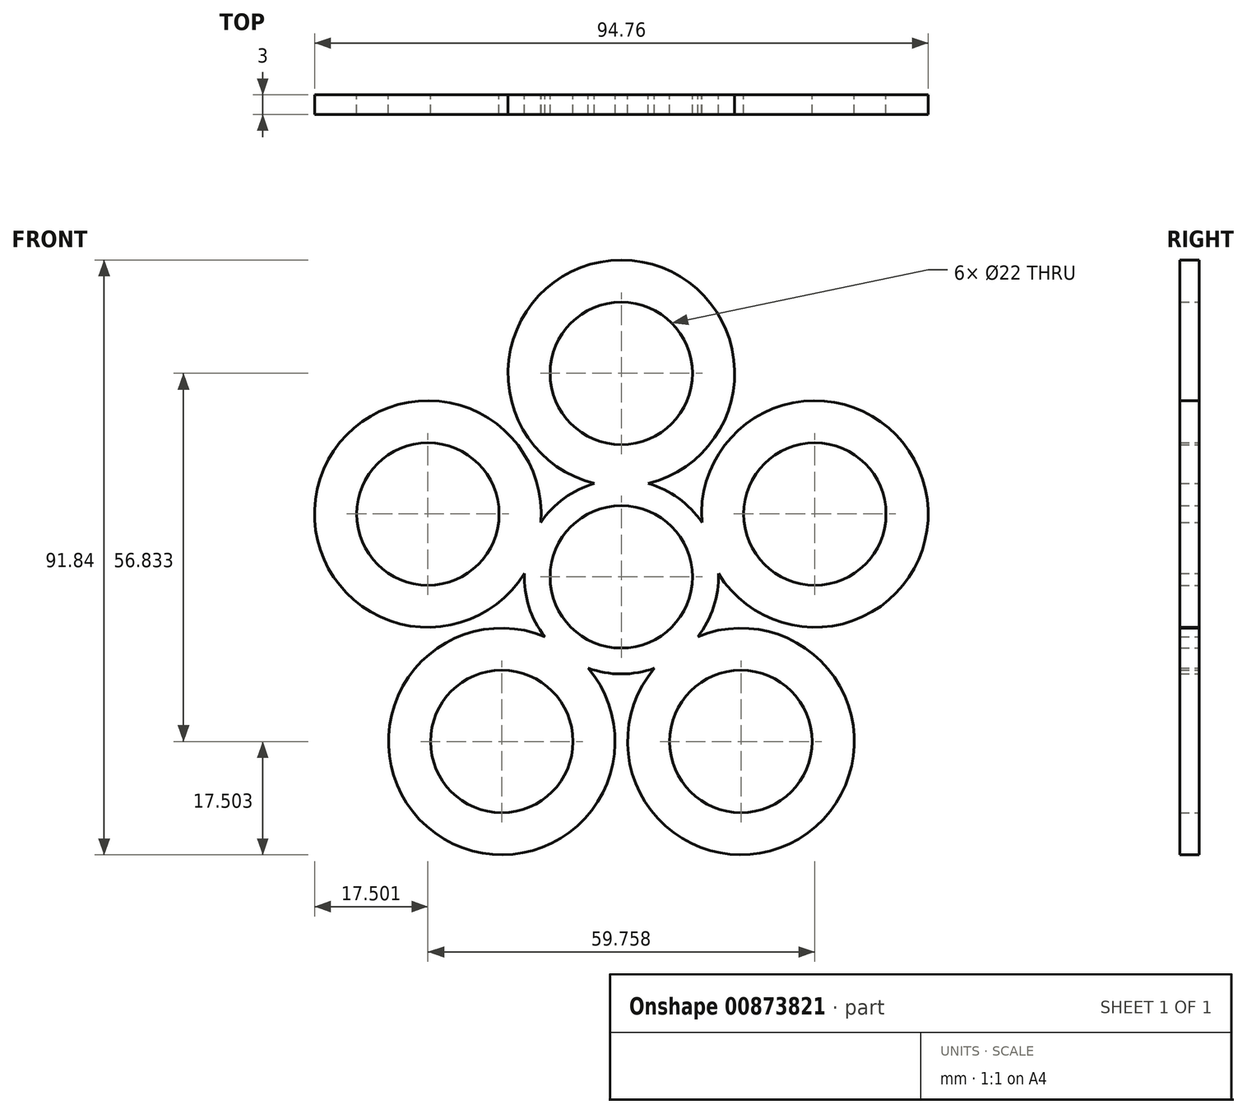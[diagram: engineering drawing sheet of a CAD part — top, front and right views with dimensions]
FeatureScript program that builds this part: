
annotation { "Feature Type Name" : "Feature", "Feature Type Description" : "" }
export const myFeature = defineFeature(function(context is Context, id is Id, definition is map)
    precondition{}
    {
        {
            var Q0;
            Q0=qCreatedBy(makeId("Front.planeOp"),FACE);
            var sketch = newSketch(context, id + "F0", { "sketchPlane" : qUnion([Q0])});
            skCircle(sketch, "E0", {"center": v(0, 0) * mm, "radius": 11 * mm});
            skCircle(sketch, "E1", {"center": v(0, 31.42) * mm, "radius": 11 * mm});
            skArc(sketch, "E2", {"start": v(-4.15, 14.42) * mm, "mid": v(-8.82, 12.14) * mm, "end": v(-12.43, 8.4) * mm});
            skArc(sketch, "E3", {"start": v(4.15, 14.42) * mm, "mid": v(0, 48.92) * mm, "end": v(-4.15, 14.42) * mm});
            skCircle(sketch, "E4.1.0", {"center": v(-29.88, 9.7) * mm, "radius": 11 * mm});
            skArc(sketch, "E4.1.1", {"start": v(-12.43, 8.4) * mm, "mid": v(-46.52, 15.12) * mm, "end": v(-15, 0.51) * mm});
            skCircle(sketch, "E4.2.0", {"center": v(-18.47, -25.42) * mm, "radius": 11 * mm});
            skArc(sketch, "E4.2.1", {"start": v(-11.83, -9.22) * mm, "mid": v(-28.75, -39.57) * mm, "end": v(-5.12, -14.1) * mm});
            skCircle(sketch, "E4.3.0", {"center": v(18.47, -25.42) * mm, "radius": 11 * mm});
            skArc(sketch, "E4.3.1", {"start": v(5.12, -14.1) * mm, "mid": v(28.75, -39.57) * mm, "end": v(11.83, -9.22) * mm});
            skCircle(sketch, "E4.4.0", {"center": v(29.88, 9.7) * mm, "radius": 11 * mm});
            skArc(sketch, "E4.4.1", {"start": v(15, 0.51) * mm, "mid": v(46.52, 15.12) * mm, "end": v(12.43, 8.4) * mm});
            skArc(sketch, "E5.trimOffspring", {"start": v(-15, 0.51) * mm, "mid": v(-14.27, -4.64) * mm, "end": v(-11.83, -9.22) * mm});
            skArc(sketch, "E6.trimOffspring", {"start": v(12.43, 8.4) * mm, "mid": v(8.82, 12.14) * mm, "end": v(4.15, 14.42) * mm});
            skArc(sketch, "E7.trimOffspring", {"start": v(11.83, -9.22) * mm, "mid": v(14.27, -4.64) * mm, "end": v(15, 0.51) * mm});
            skArc(sketch, "E8.trimOffspring", {"start": v(-5.12, -14.1) * mm, "mid": v(0, -15) * mm, "end": v(5.12, -14.1) * mm});
            skSolve(sketch);
        }
        {
            var Q0;
            Q0 = qSketchRegion(id + "F0", true);
            extrude(context, id + "F1", {"entities" : qUnion([Q0]), "depth" : 3 * mm, "offsetDistance" : 25 * mm});
        }
    });
